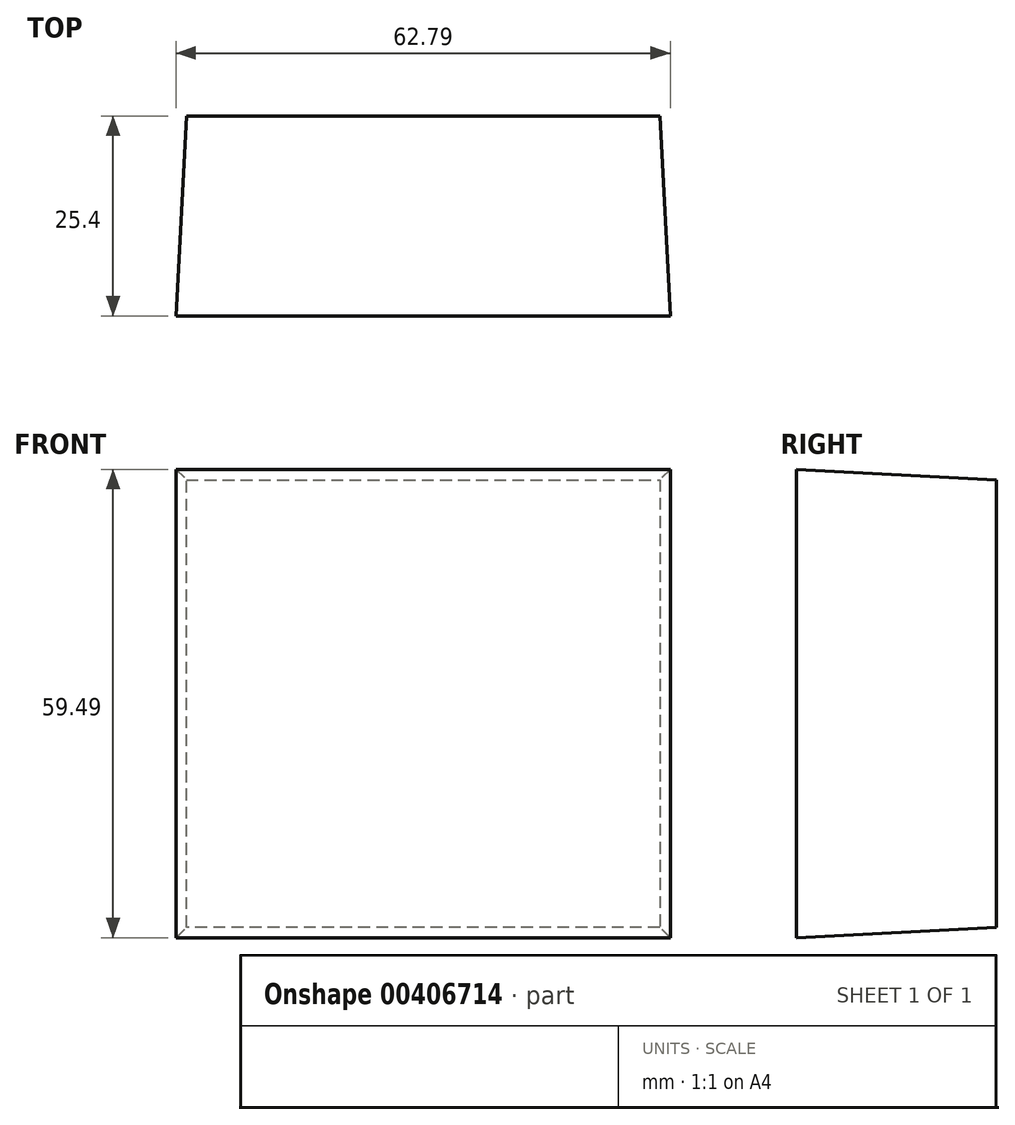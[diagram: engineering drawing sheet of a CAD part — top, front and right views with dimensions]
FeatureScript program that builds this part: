
annotation { "Feature Type Name" : "Feature", "Feature Type Description" : "" }
export const myFeature = defineFeature(function(context is Context, id is Id, definition is map)
    precondition{}
    {
        {
            var Q0;
            Q0=qCreatedBy(makeId("Front.planeOp"),FACE);
            var sketch = newSketch(context, id + "F0", { "sketchPlane" : qUnion([Q0])});
            skLineSegment(sketch, "E0", {"start": v(0, 0) * mm, "end": v(0, 56.83) * mm});
            skLineSegment(sketch, "E1", {"start": v(0, 56.83) * mm, "end": v(60.13, 56.83) * mm});
            skLineSegment(sketch, "E2", {"start": v(60.13, 56.83) * mm, "end": v(60.13, 0) * mm});
            skLineSegment(sketch, "E3", {"start": v(60.13, 0) * mm, "end": v(60.13, 0) * mm});
            skLineSegment(sketch, "E4", {"start": v(60.13, 0) * mm, "end": v(0, 0) * mm});
            skSolve(sketch);
        }
        {
            var Q0;
            Q0=makeQuery(id+"F0.imprint","IMPRINT",FACE,{"disambiguationData":[TD([[makeQuery(id+"F0.imprint","IMPRINT",EDGE,{"derivedFrom":sQuery(id+"F0.wireOp",EDGE,"E0")}),-1.0]])]});
            extrude(context, id + "F1", {"entities" : qUnion([Q0]), "depth" : 25.4 * mm, "hasDraft" : true, "draftAngle" : 3 * degree});
        }
    });
